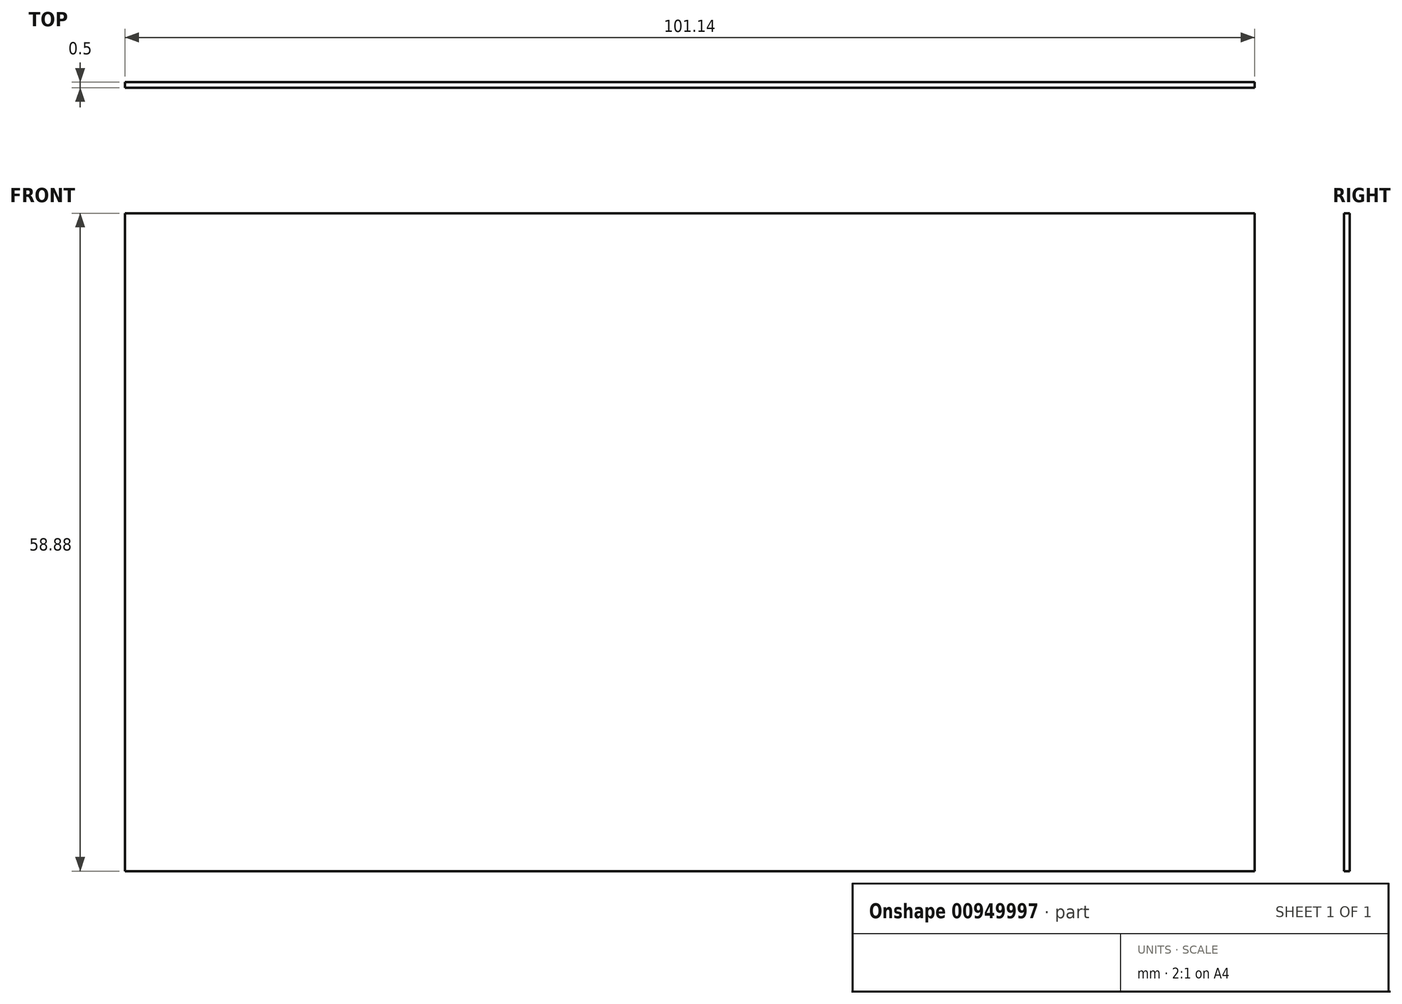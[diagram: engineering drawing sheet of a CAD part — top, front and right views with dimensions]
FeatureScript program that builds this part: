
annotation { "Feature Type Name" : "Feature", "Feature Type Description" : "" }
export const myFeature = defineFeature(function(context is Context, id is Id, definition is map)
    precondition{}
    {
        {
            var Q0;
            Q0=qCreatedBy(makeId("Front.planeOp"),FACE);
            var sketch = newSketch(context, id + "F0", { "sketchPlane" : qUnion([Q0])});
            skLineSegment(sketch, "E0.bottom", {"start": v(50.57, -29.44) * mm, "end": v(-50.57, -29.44) * mm});
            skLineSegment(sketch, "E0.top", {"start": v(50.57, 29.44) * mm, "end": v(-50.57, 29.44) * mm});
            skLineSegment(sketch, "E0.left", {"start": v(50.57, -29.44) * mm, "end": v(50.57, 29.44) * mm});
            skLineSegment(sketch, "E0.right", {"start": v(-50.57, -29.44) * mm, "end": v(-50.57, 29.44) * mm});
            skPoint(sketch, "E0.middle", {"position": v(0, 0) * mm});
            skSolve(sketch);
        }
        {
            var Q0;
            Q0 = qSketchRegion(id + "F0", true);
            extrude(context, id + "F1", {"entities" : qUnion([Q0]), "depth" : 0.25 * mm, "offsetDistance" : 25.4 * mm});
        }
        {
            var Q0;
            Q0=makeQuery(id+"F0.imprint","IMPRINT",FACE,{"disambiguationData":[TD([[makeQuery(id+"F0.imprint","IMPRINT",EDGE,{"derivedFrom":sQuery(id+"F0.wireOp",EDGE,"E0.bottom")}),-1.0]])]});
            extrude(context, id + "F2", {"entities" : qUnion([Q0]), "operationType" : NewBodyOperationType.ADD, "oppositeDirection" : true, "depth" : 0.25 * mm, "offsetDistance" : 25.4 * mm});
        }
    });
